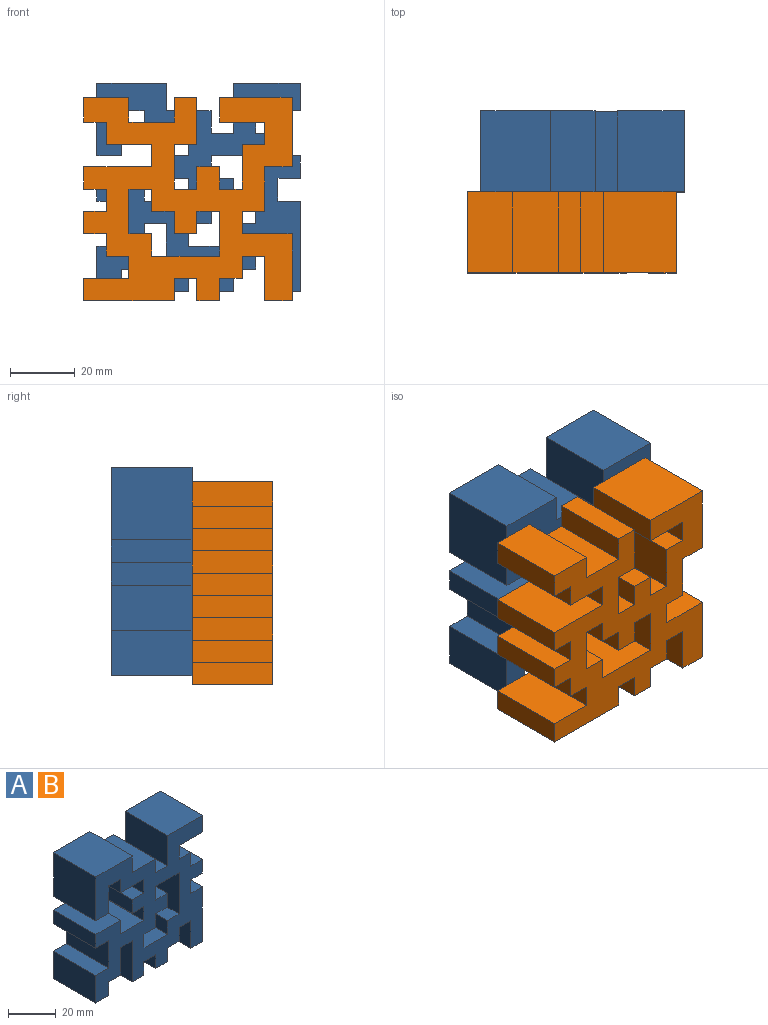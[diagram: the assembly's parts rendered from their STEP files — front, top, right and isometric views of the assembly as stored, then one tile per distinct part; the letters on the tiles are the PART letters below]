
ASSEMBLY  parts=2 mates=1
PART A: 68 faces, bbox 62.9x25x64.4 mm
  f0: plane 25x7mm, normal (1,0,0), area 175mm2, adj f1,f65,f66,f67
  f1: plane 25x13.8mm, normal (0,0,-1), area 345mm2, adj f0,f2,f66,f67
  f2: plane 25x21mm, normal (-1,0,0), area 525mm2, adj f1,f3,f66,f67
  f3: plane 25x6.9mm, normal (0,0,1), area 172.5mm2, adj f2,f4,f66,f67
  f4: plane 25x7mm, normal (-1,0,0), area 175mm2, adj f3,f5,f66,f67
  f5: plane 25x13.8mm, normal (0,0,1), area 345mm2, adj f4,f6,f66,f67
  f6: plane 25x7mm, normal (1,0,0), area 175mm2, adj f5,f7,f66,f67
  f7: plane 25x6.9mm, normal (0,0,-1), area 172.5mm2, adj f6,f8,f66,f67
  f8: plane 25x7mm, normal (1,0,0), area 175mm2, adj f7,f9,f66,f67
  f9: plane 25x6.9mm, normal (0,0,-1), area 172.5mm2, adj f8,f10,f66,f67
  f10: plane 25x7mm, normal (1,0,0), area 175mm2, adj f9,f65,f66,f67
  f11: plane 25x21.48mm, normal (0,0,1), area 537mm2, adj f12,f64,f66,f67
  f12: plane 25x22.42mm, normal (-1,0,0), area 560.5mm2, adj f11,f13,f66,f67
  f13: plane 25x7.68mm, normal (0,0,-1), area 192mm2, adj f12,f14,f66,f67
  f14: plane 25x14mm, normal (1,0,0), area 350mm2, adj f13,f15,f66,f67
  f15: plane 25x6.9mm, normal (0,0,-1), area 172.5mm2, adj f14,f16,f66,f67
  f16: plane 25x7mm, normal (-1,0,0), area 175mm2, adj f15,f17,f66,f67
  f17: plane 25x13.8mm, normal (0,0,-1), area 345mm2, adj f16,f18,f66,f67
  f18: plane 25x7mm, normal (-1,0,0), area 175mm2, adj f17,f19,f66,f67
  f19: plane 25x6.9mm, normal (0,0,1), area 172.5mm2, adj f18,f20,f66,f67
  f20: plane 25x7mm, normal (-1,0,0), area 175mm2, adj f19,f21,f66,f67
  f21: plane 25x6.9mm, normal (0,0,-1), area 172.5mm2, adj f20,f22,f66,f67
  f22: plane 25x7mm, normal (-1,0,0), area 175mm2, adj f21,f23,f66,f67
  f23: plane 25x13.8mm, normal (0,0,1), area 345mm2, adj f22,f24,f66,f67
  f24: plane 25x7mm, normal (1,0,0), area 175mm2, adj f23,f25,f66,f67
  f25: plane 25x14.58mm, normal (0,0,1), area 364.5mm2, adj f24,f26,f66,f67
  f26: plane 25x7mm, normal (-1,0,0), area 175mm2, adj f25,f27,f66,f67
  f27: plane 25x7.68mm, normal (0,0,-1), area 192mm2, adj f26,f28,f66,f67
  f28: plane 25x14mm, normal (-1,0,0), area 350mm2, adj f27,f29,f66,f67
  f29: plane 25x7.68mm, normal (0,0,1), area 192mm2, adj f28,f30,f66,f67
  f30: plane 25x14mm, normal (-1,0,0), area 350mm2, adj f29,f31,f66,f67
  f31: plane 25x7.68mm, normal (0,0,-1), area 192mm2, adj f30,f32,f66,f67
  f32: plane 25x7mm, normal (1,0,0), area 175mm2, adj f31,f33,f66,f67
  f33: plane 25x6.9mm, normal (0,0,-1), area 172.5mm2, adj f32,f34,f66,f67
  f34: plane 25x14mm, normal (1,0,0), area 350mm2, adj f33,f35,f66,f67
  f35: plane 25x6.9mm, normal (0,0,-1), area 172.5mm2, adj f34,f36,f66,f67
  f36: plane 25x21mm, normal (-1,0,0), area 525mm2, adj f35,f37,f66,f67
  f37: plane 25x6.9mm, normal (0,0,-1), area 172.5mm2, adj f36,f38,f66,f67
  f38: plane 25x7mm, normal (1,0,0), area 175mm2, adj f37,f39,f66,f67
  f39: plane 25x6.9mm, normal (0,0,-1), area 172.5mm2, adj f38,f40,f66,f67
  f40: plane 25x7mm, normal (-1,0,0), area 175mm2, adj f39,f41,f66,f67
  f41: plane 25x6.9mm, normal (0,0,-1), area 172.5mm2, adj f40,f42,f66,f67
  f42: plane 25x7mm, normal (1,0,0), area 175mm2, adj f41,f43,f66,f67
  f43: plane 25x6.9mm, normal (0,0,-1), area 172.5mm2, adj f42,f44,f66,f67
  f44: plane 25x7mm, normal (1,0,0), area 175mm2, adj f43,f45,f66,f67
  f45: plane 25x6.9mm, normal (0,0,-1), area 172.5mm2, adj f44,f46,f66,f67
  f46: plane 25x14mm, normal (-1,0,0), area 350mm2, adj f45,f47,f66,f67
  f47: plane 25x6.9mm, normal (0,0,-1), area 172.5mm2, adj f46,f48,f66,f67
  f48: plane 28x25mm, normal (1,0,0), area 700mm2, adj f47,f49,f66,f67
  f49: plane 25x6.9mm, normal (0,0,1), area 172.5mm2, adj f48,f50,f66,f67
  f50: plane 25x7mm, normal (1,0,0), area 175mm2, adj f49,f51,f66,f67
  f51: plane 25x6.9mm, normal (0,0,-1), area 172.5mm2, adj f50,f52,f66,f67
  f52: plane 25x7mm, normal (1,0,0), area 175mm2, adj f51,f53,f66,f67
  f53: plane 25x6.9mm, normal (0,0,1), area 172.5mm2, adj f52,f54,f66,f67
  f54: plane 25x7mm, normal (1,0,0), area 175mm2, adj f53,f55,f66,f67
  f55: plane 25x6.9mm, normal (0,0,1), area 172.5mm2, adj f54,f56,f66,f67
  f56: plane 25x7mm, normal (1,0,0), area 175mm2, adj f55,f57,f66,f67
  f57: plane 25x13.8mm, normal (0,0,-1), area 345mm2, adj f56,f58,f66,f67
  f58: plane 25x8.42mm, normal (1,0,0), area 210.5mm2, adj f57,f59,f66,f67
  f59: plane 25x20.7mm, normal (0,0,1), area 517.5mm2, adj f58,f60,f66,f67
  f60: plane 25x15.42mm, normal (-1,0,0), area 385.5mm2, adj f59,f61,f66,f67
  f61: plane 25x6.9mm, normal (0,0,1), area 172.5mm2, adj f60,f62,f66,f67
  f62: plane 25x7mm, normal (1,0,0), area 175mm2, adj f61,f63,f66,f67
  f63: plane 25x13.8mm, normal (0,0,1), area 345mm2, adj f62,f64,f66,f67
  f64: plane 25x8.42mm, normal (1,0,0), area 210.5mm2, adj f11,f63,f66,f67
  f65: plane 25x6.9mm, normal (0,0,1), area 172.5mm2, adj f0,f10,f66,f67
  f66: plane 64.42x62.88mm, normal (0,-1,0), area 2362.8mm2, adj f0,f1,f2,f3,f4,f5,f6,f7
  f67: plane 64.42x62.88mm, normal (0,1,0), area 2362.8mm2, adj f0,f1,f2,f3,f4,f5,f6,f7
PART B: same geometry as A
PLACE A t=(-35.62,-15.75,-2.51)mm
PLACE B rot(axis=(0,1,0),90deg) t=(24.72,-40.75,-6.85)mm
MATE planar B.f67 <-> A.f66  axis (0,1,0) through (-18.7,-40.75,-55.93)mm
